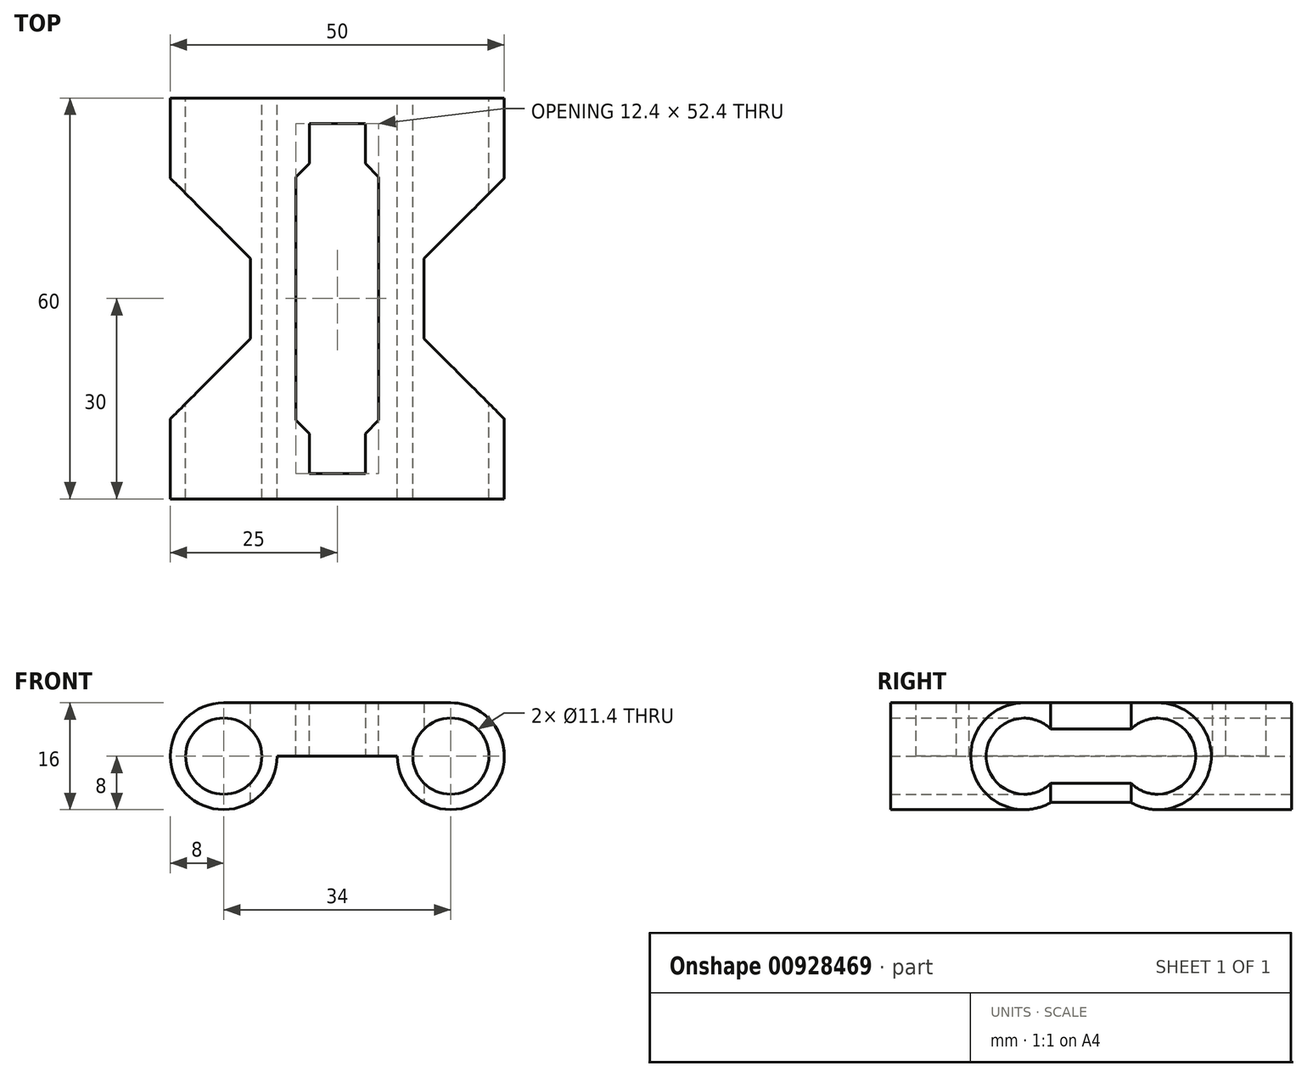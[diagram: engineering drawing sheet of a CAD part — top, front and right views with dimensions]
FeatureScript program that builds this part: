
annotation { "Feature Type Name" : "Feature", "Feature Type Description" : "" }
export const myFeature = defineFeature(function(context is Context, id is Id, definition is map)
    precondition{}
    {
        {
            var Q0;
            Q0=qCreatedBy(makeId("Front.planeOp"),FACE);
            var sketch = newSketch(context, id + "F0", { "sketchPlane" : qUnion([Q0])});
            skCircle(sketch, "E0", {"center": v(0, 0) * mm, "radius": 5.7 * mm});
            skCircle(sketch, "E1", {"center": v(0, 0) * mm, "radius": 8 * mm});
            skLineSegment(sketch, "E2", {"start": v(0, 8) * mm, "end": v(34, 8) * mm});
            skLineSegment(sketch, "E3", {"start": v(8, 0) * mm, "end": v(26, 0) * mm});
            skPoint(sketch, "E4", {"position": v(34, 0) * mm});
            skCircle(sketch, "E5", {"center": v(34, 0) * mm, "radius": 8 * mm});
            skCircle(sketch, "E6", {"center": v(34, 0) * mm, "radius": 5.7 * mm});
            skSolve(sketch);
        }
        {
            var Q0;
            Q0=makeQuery(id+"F0.imprint","IMPRINT",FACE,{"disambiguationData":[TD([[makeQuery(id+"F0.imprint","IMPRINT",EDGE,{"derivedFrom":sQuery(id+"F0.wireOp",EDGE,"E0")}),-1.0]])]});
            var Q1;
            {var subQ0=sQuery(id+"F0.wireOp",EDGE,"E2");Q1=makeQuery(id+"F0.imprint","IMPRINT",FACE,{"disambiguationData":[TD([[makeQuery(id+"F0.imprint","IMPRINT",EDGE,{"derivedFrom":subQ0}),-1.0]])]});}
            var Q2;
            Q2=makeQuery(id+"F0.imprint","IMPRINT",FACE,{"disambiguationData":[TD([[makeQuery(id+"F0.imprint","IMPRINT",EDGE,{"derivedFrom":sQuery(id+"F0.wireOp",EDGE,"E6")}),-1.0]])]});
            extrude(context, id + "F1", {"entities" : qUnion([Q0, Q1, Q2]), "depth" : 60 * mm, "offsetDistance" : 25 * mm});
        }
        {
            var Q0;
            Q0=makeQuery(id+"F1.opExtrude","SWEPT_FACE",FACE,{"disambiguationData":[OSD([sQuery(id+"F0.wireOp",EDGE,"E2")])]});
            var sketch = newSketch(context, id + "F2", { "sketchPlane" : qUnion([Q0])});
            skLineSegment(sketch, "E7.bottom", {"start": v(12.8, -3.8) * mm, "end": v(21.2, -3.8) * mm});
            skLineSegment(sketch, "E7.top", {"start": v(12.8, -56.2) * mm, "end": v(21.2, -56.2) * mm});
            skLineSegment(sketch, "E7.left", {"start": v(12.8, -3.8) * mm, "end": v(12.8, -56.2) * mm});
            skLineSegment(sketch, "E7.right", {"start": v(21.2, -3.8) * mm, "end": v(21.2, -56.2) * mm});
            skLineSegment(sketch, "E8.bottom", {"start": v(12.8, -11.8) * mm, "end": v(10.8, -11.8) * mm});
            skLineSegment(sketch, "E8.top", {"start": v(12.8, -48.2) * mm, "end": v(10.8, -48.2) * mm});
            skLineSegment(sketch, "E8.left", {"start": v(12.8, -11.8) * mm, "end": v(12.8, -48.2) * mm});
            skLineSegment(sketch, "E8.right", {"start": v(10.8, -11.8) * mm, "end": v(10.8, -48.2) * mm});
            skLineSegment(sketch, "E9.bottom", {"start": v(21.2, -11.8) * mm, "end": v(23.2, -11.8) * mm});
            skLineSegment(sketch, "E9.top", {"start": v(21.2, -48.2) * mm, "end": v(23.2, -48.2) * mm});
            skLineSegment(sketch, "E9.left", {"start": v(21.2, -11.8) * mm, "end": v(21.2, -48.2) * mm});
            skLineSegment(sketch, "E9.right", {"start": v(23.2, -11.8) * mm, "end": v(23.2, -48.2) * mm});
            skSolve(sketch);
        }
        {
            var Q0;
            {var subQ3=sQuery(id+"F2.wireOp",EDGE,"E7.bottom");Q0=makeQuery(id+"F2.imprint","IMPRINT",FACE,{"disambiguationData":[TD([[makeQuery(id+"F2.imprint","IMPRINT",EDGE,{"derivedFrom":subQ3}),-1.0]])]});}
            var Q1;
            Q1=makeQuery(id+"F2.imprint","IMPRINT",FACE,{"disambiguationData":[TD([[makeQuery(id+"F2.imprint","IMPRINT",EDGE,{"derivedFrom":sQuery(id+"F2.wireOp",EDGE,"E9.bottom")}),-1.0]])]});
            var Q2;
            Q2=makeQuery(id+"F2.imprint","IMPRINT",FACE,{"disambiguationData":[TD([[makeQuery(id+"F2.imprint","IMPRINT",EDGE,{"derivedFrom":sQuery(id+"F2.wireOp",EDGE,"E8.bottom")}),1.0]])]});
            extrude(context, id + "F3", {"entities" : qUnion([Q0, Q1, Q2]), "operationType" : NewBodyOperationType.REMOVE, "oppositeDirection" : true, "depth" : 25 * mm, "offsetDistance" : 25 * mm});
        }
        {
            var Q0;
            Q0=makeQuery(id+"F1.opExtrude","SWEPT_FACE",FACE,{"disambiguationData":[OSD([sQuery(id+"F0.wireOp",EDGE,"E2")])]});
            var sketch = newSketch(context, id + "F4", { "sketchPlane" : qUnion([Q0])});
            skLineSegment(sketch, "E10", {"start": v(34, -60) * mm, "end": v(34, -48) * mm});
            skLineSegment(sketch, "E11", {"start": v(34, -48) * mm, "end": v(42, -48) * mm});
            skLineSegment(sketch, "E12", {"start": v(42, -48) * mm, "end": v(42, -12) * mm});
            skLineSegment(sketch, "E13", {"start": v(42, -12) * mm, "end": v(34, -12) * mm});
            skLineSegment(sketch, "E14", {"start": v(34, -12) * mm, "end": v(30, -12) * mm});
            skLineSegment(sketch, "E15", {"start": v(30, -12) * mm, "end": v(30, -48) * mm});
            skLineSegment(sketch, "E16", {"start": v(30, -48) * mm, "end": v(34, -48) * mm});
            skLineSegment(sketch, "E17", {"start": v(0, -60) * mm, "end": v(0, -48) * mm});
            skLineSegment(sketch, "E18", {"start": v(0, -48) * mm, "end": v(4, -48) * mm});
            skLineSegment(sketch, "E19", {"start": v(4, -48) * mm, "end": v(4, -12) * mm});
            skLineSegment(sketch, "E20", {"start": v(4, -12) * mm, "end": v(0, -12) * mm});
            skLineSegment(sketch, "E21", {"start": v(0, -12) * mm, "end": v(-8, -12) * mm});
            skLineSegment(sketch, "E22", {"start": v(-8, -12) * mm, "end": v(-8, -48) * mm});
            skLineSegment(sketch, "E23", {"start": v(-8, -48) * mm, "end": v(0, -48) * mm});
            skSolve(sketch);
        }
        {
            var Q0;
            {var subQ0=sQuery(id+"F4.wireOp",EDGE,"E11");Q0=makeQuery(id+"F4.imprint","IMPRINT",FACE,{"disambiguationData":[TD([[makeQuery(id+"F4.imprint","IMPRINT",EDGE,{"derivedFrom":subQ0}),1.0]])]});}
            var Q1;
            {var subQ0=sQuery(id+"F4.wireOp",EDGE,"E14");Q1=makeQuery(id+"F4.imprint","IMPRINT",FACE,{"disambiguationData":[TD([[makeQuery(id+"F4.imprint","IMPRINT",EDGE,{"derivedFrom":subQ0}),1.0]])]});}
            var Q2;
            {var subQ0=sQuery(id+"F4.wireOp",EDGE,"E21");Q2=makeQuery(id+"F4.imprint","IMPRINT",FACE,{"disambiguationData":[TD([[makeQuery(id+"F4.imprint","IMPRINT",EDGE,{"derivedFrom":subQ0}),1.0]])]});}
            var Q3;
            {var subQ0=sQuery(id+"F4.wireOp",EDGE,"E18");Q3=makeQuery(id+"F4.imprint","IMPRINT",FACE,{"disambiguationData":[TD([[makeQuery(id+"F4.imprint","IMPRINT",EDGE,{"derivedFrom":subQ0}),1.0]])]});}
            extrude(context, id + "F5", {"entities" : qUnion([Q0, Q1, Q2, Q3]), "operationType" : NewBodyOperationType.REMOVE, "oppositeDirection" : true, "depth" : 25 * mm, "offsetDistance" : 25 * mm});
        }
        {
            var Q0;
            {var subQ0=sQuery(id+"F4.wireOp",EDGE,"E14");var subQ1=sQuery(id+"F4.wireOp",EDGE,"E15");Q0=makeQuery(id+"F5.boolean.opBoolean","COPY",EDGE,{"disambiguationData":[TD([makeQuery(id+"F1.opExtrude","SWEPT_FACE",FACE,{"disambiguationData":[OSD([sQuery(id+"F0.wireOp",EDGE,"E2")])]})])],"derivedFrom":makeQuery(id+"F5.opExtrude","SWEPT_EDGE",EDGE,{"disambiguationData":[OSD([subQ0,subQ1])]})});}
            var Q1;
            {var subQ0=sQuery(id+"F4.wireOp",EDGE,"E14");var subQ1=sQuery(id+"F4.wireOp",EDGE,"E15");Q1=makeQuery(id+"F5.boolean.opBoolean","COPY",EDGE,{"disambiguationData":[TD([makeQuery(id+"F1.opExtrude","SWEPT_FACE",FACE,{"disambiguationData":[OSD([sQuery(id+"F0.wireOp",EDGE,"E5")])]})])],"derivedFrom":makeQuery(id+"F5.opExtrude","SWEPT_EDGE",EDGE,{"disambiguationData":[OSD([subQ0,subQ1])]})});}
            var Q2;
            {var subQ0=sQuery(id+"F4.wireOp",EDGE,"E16");var subQ1=sQuery(id+"F4.wireOp",EDGE,"E15");Q2=makeQuery(id+"F5.boolean.opBoolean","COPY",EDGE,{"disambiguationData":[TD([makeQuery(id+"F1.opExtrude","SWEPT_FACE",FACE,{"disambiguationData":[OSD([sQuery(id+"F0.wireOp",EDGE,"E5")])]})])],"derivedFrom":makeQuery(id+"F5.opExtrude","SWEPT_EDGE",EDGE,{"disambiguationData":[OSD([subQ1,subQ0])]})});}
            var Q3;
            {var subQ0=sQuery(id+"F4.wireOp",EDGE,"E16");var subQ1=sQuery(id+"F4.wireOp",EDGE,"E15");Q3=makeQuery(id+"F5.boolean.opBoolean","COPY",EDGE,{"disambiguationData":[TD([makeQuery(id+"F1.opExtrude","SWEPT_FACE",FACE,{"disambiguationData":[OSD([sQuery(id+"F0.wireOp",EDGE,"E2")])]})])],"derivedFrom":makeQuery(id+"F5.opExtrude","SWEPT_EDGE",EDGE,{"disambiguationData":[OSD([subQ1,subQ0])]})});}
            var Q4;
            {var subQ0=sQuery(id+"F4.wireOp",EDGE,"E18");var subQ1=sQuery(id+"F4.wireOp",EDGE,"E19");Q4=makeQuery(id+"F5.boolean.opBoolean","COPY",EDGE,{"disambiguationData":[TD([makeQuery(id+"F1.opExtrude","SWEPT_FACE",FACE,{"disambiguationData":[OSD([sQuery(id+"F0.wireOp",EDGE,"E2")])]})])],"derivedFrom":makeQuery(id+"F5.opExtrude","SWEPT_EDGE",EDGE,{"disambiguationData":[OSD([subQ0,subQ1])]})});}
            var Q5;
            {var subQ0=sQuery(id+"F4.wireOp",EDGE,"E18");var subQ1=sQuery(id+"F4.wireOp",EDGE,"E19");Q5=makeQuery(id+"F5.boolean.opBoolean","COPY",EDGE,{"disambiguationData":[TD([makeQuery(id+"F1.opExtrude","SWEPT_FACE",FACE,{"disambiguationData":[OSD([sQuery(id+"F0.wireOp",EDGE,"E1")])]})])],"derivedFrom":makeQuery(id+"F5.opExtrude","SWEPT_EDGE",EDGE,{"disambiguationData":[OSD([subQ0,subQ1])]})});}
            var Q6;
            {var subQ0=sQuery(id+"F4.wireOp",EDGE,"E19");var subQ1=sQuery(id+"F4.wireOp",EDGE,"E20");Q6=makeQuery(id+"F5.boolean.opBoolean","COPY",EDGE,{"disambiguationData":[TD([makeQuery(id+"F1.opExtrude","SWEPT_FACE",FACE,{"disambiguationData":[OSD([sQuery(id+"F0.wireOp",EDGE,"E2")])]})])],"derivedFrom":makeQuery(id+"F5.opExtrude","SWEPT_EDGE",EDGE,{"disambiguationData":[OSD([subQ0,subQ1])]})});}
            var Q7;
            {var subQ0=sQuery(id+"F4.wireOp",EDGE,"E20");var subQ1=sQuery(id+"F4.wireOp",EDGE,"E19");Q7=makeQuery(id+"F5.boolean.opBoolean","COPY",EDGE,{"disambiguationData":[TD([makeQuery(id+"F1.opExtrude","SWEPT_FACE",FACE,{"disambiguationData":[OSD([sQuery(id+"F0.wireOp",EDGE,"E1")])]})])],"derivedFrom":makeQuery(id+"F5.opExtrude","SWEPT_EDGE",EDGE,{"disambiguationData":[OSD([subQ1,subQ0])]})});}
            chamfer(context, id + "F6", {"entities" : qUnion([Q0, Q1, Q2, Q3, Q4, Q5, Q6, Q7]), "width" : 12 * mm, "tangentPropagation" : true});
        }
        {
            var Q0;
            Q0=makeQuery(id+"F3.boolean.opBoolean","COPY",EDGE,{"derivedFrom":makeQuery(id+"F3.opExtrude","SWEPT_EDGE",EDGE,{"disambiguationData":[OSD([sQuery(id+"F2.wireOp",EDGE,"E7.left"),sQuery(id+"F2.wireOp",EDGE,"E8.bottom"),sQuery(id+"F2.wireOp",EDGE,"E8.left")])]})});
            var Q1;
            Q1=makeQuery(id+"F3.boolean.opBoolean","COPY",EDGE,{"derivedFrom":makeQuery(id+"F3.opExtrude","SWEPT_EDGE",EDGE,{"disambiguationData":[OSD([sQuery(id+"F2.wireOp",EDGE,"E7.right"),sQuery(id+"F2.wireOp",EDGE,"E9.bottom"),sQuery(id+"F2.wireOp",EDGE,"E9.left")])]})});
            var Q2;
            Q2=makeQuery(id+"F3.boolean.opBoolean","COPY",EDGE,{"derivedFrom":makeQuery(id+"F3.opExtrude","SWEPT_EDGE",EDGE,{"disambiguationData":[OSD([sQuery(id+"F2.wireOp",EDGE,"E7.left"),sQuery(id+"F2.wireOp",EDGE,"E8.top"),sQuery(id+"F2.wireOp",EDGE,"E8.left")])]})});
            var Q3;
            Q3=makeQuery(id+"F3.boolean.opBoolean","COPY",EDGE,{"derivedFrom":makeQuery(id+"F3.opExtrude","SWEPT_EDGE",EDGE,{"disambiguationData":[OSD([sQuery(id+"F2.wireOp",EDGE,"E7.right"),sQuery(id+"F2.wireOp",EDGE,"E9.top"),sQuery(id+"F2.wireOp",EDGE,"E9.left")])]})});
            chamfer(context, id + "F7", {"entities" : qUnion([Q0, Q1, Q2, Q3]), "width" : 2 * mm, "tangentPropagation" : true});
        }
    });
